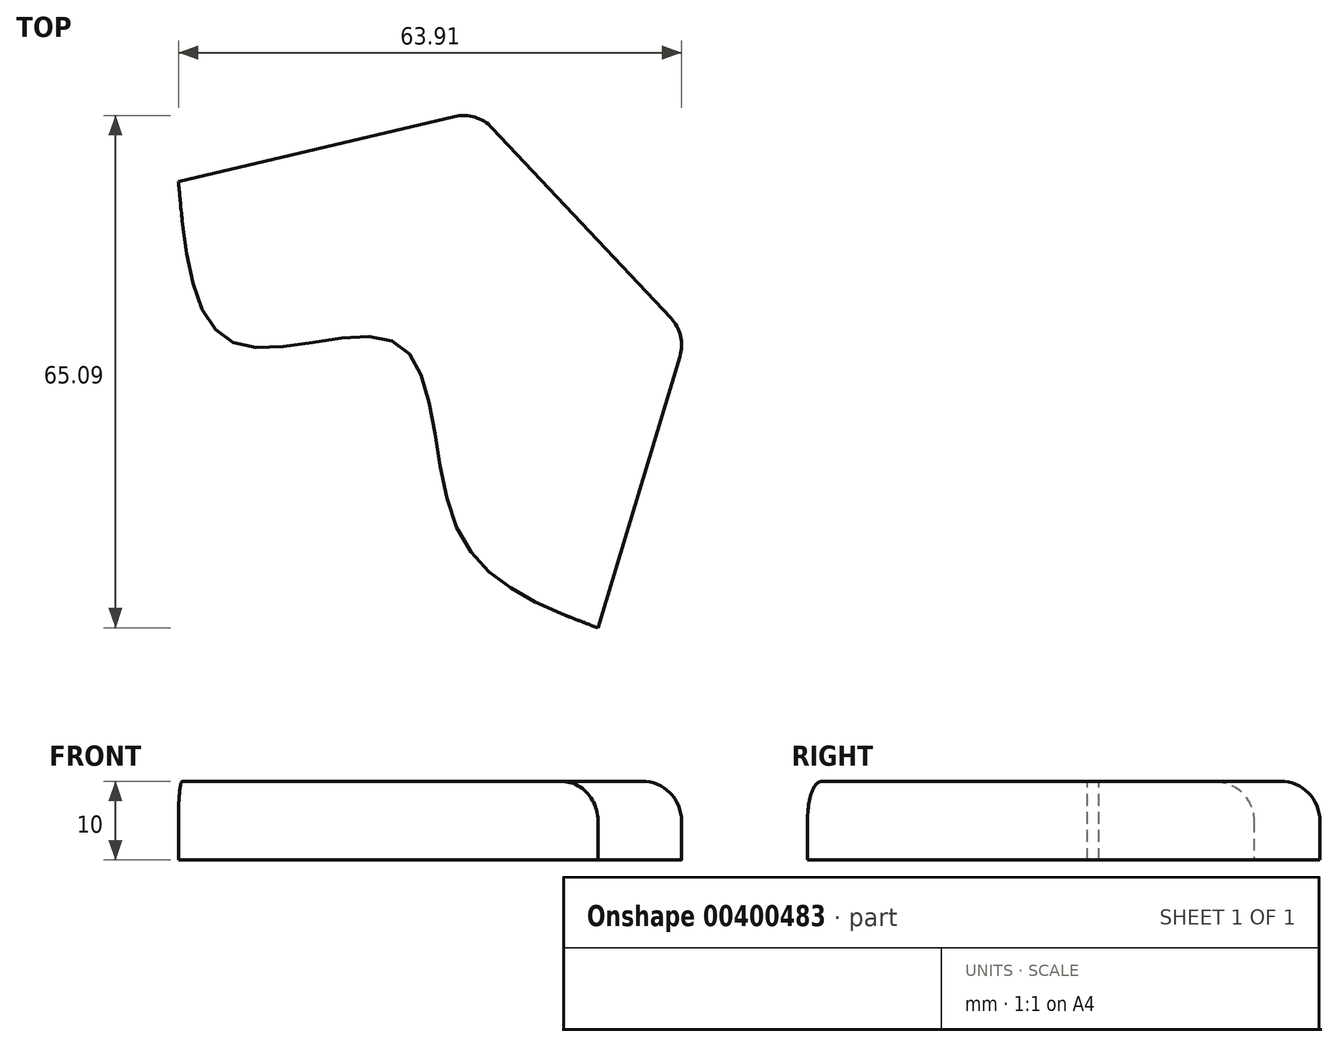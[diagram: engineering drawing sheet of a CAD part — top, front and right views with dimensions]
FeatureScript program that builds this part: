
annotation { "Feature Type Name" : "Feature", "Feature Type Description" : "" }
export const myFeature = defineFeature(function(context is Context, id is Id, definition is map)
    precondition{}
    {
        {
            var Q0;
            Q0=qCreatedBy(makeId("Top.planeOp"),FACE);
            var sketch = newSketch(context, id + "F0", { "sketchPlane" : qUnion([Q0])});
            skArc(sketch, "E0.cCircle", {"start": v(-79.2, -33.9) * mm, "mid": v(-76.4, 15.99) * mm, "end": v(-126.32, 13.83) * mm, "construction": true});
            skLineSegment(sketch, "E0.0", {"start": v(-127.03, 20.67) * mm, "end": v(-89.15, 29.57) * mm});
            skLineSegment(sketch, "E0.1", {"start": v(-89.15, 29.57) * mm, "end": v(-62.5, 1.2) * mm});
            skLineSegment(sketch, "E0.2", {"start": v(-62.5, 1.2) * mm, "end": v(-73.73, -36.05) * mm});
            skPoint(sketch, "E0.0.midPoint", {"position": v(-108.09, 25.12) * mm});
            skFitSpline(sketch, "E1", {"points": [v(-127.03, 20.67) * mm, v(-119.56, 0) * mm, v(-99.07, 0) * mm, v(-91.64, -23.34) * mm, v(-73.73, -36.05) * mm], "startDerivative": vector(10.27, -112.52) * mm, "endDerivative": vector(88.61, -33.29) * mm});
            skSolve(sketch);
        }
        {
            var Q0;
            Q0=makeQuery(id+"F0.imprint","IMPRINT",FACE,{"disambiguationData":[TD([[makeQuery(id+"F0.imprint","IMPRINT",EDGE,{"derivedFrom":sQuery(id+"F0.wireOp",EDGE,"E0.0")}),-1.0]])]});
            extrude(context, id + "F1", {"entities" : qUnion([Q0]), "depth" : 10 * mm});
        }
        {
            var Q0;
            Q0=makeQuery(id+"F1.opExtrude","CAP_EDGE",EDGE,{"disambiguationData":[OSD([sQuery(id+"F0.wireOp",EDGE,"E0.2")])],"isStart":false});
            var Q1;
            Q1=makeQuery(id+"F1.opExtrude","CAP_EDGE",EDGE,{"disambiguationData":[OSD([sQuery(id+"F0.wireOp",EDGE,"E0.1")])],"isStart":false});
            var Q2;
            Q2=makeQuery(id+"F1.opExtrude","CAP_EDGE",EDGE,{"disambiguationData":[OSD([sQuery(id+"F0.wireOp",EDGE,"E0.0")])],"isStart":false});
            var Q3;
            Q3=makeQuery(id+"F1.opExtrude","SWEPT_EDGE",EDGE,{"disambiguationData":[OSD([sQuery(id+"F0.wireOp",EDGE,"E0.1"),sQuery(id+"F0.wireOp",EDGE,"E0.2")])]});
            var Q4;
            Q4=makeQuery(id+"F1.opExtrude","SWEPT_EDGE",EDGE,{"disambiguationData":[OSD([sQuery(id+"F0.wireOp",EDGE,"E0.0"),sQuery(id+"F0.wireOp",EDGE,"E0.1")])]});
            fillet(context, id + "F2", {"entities" : qUnion([Q0, Q1, Q2, Q3, Q4]), "radius" : 5 * mm, "tangentPropagation" : true, "allowEdgeOverflow" : false});
        }
    });
